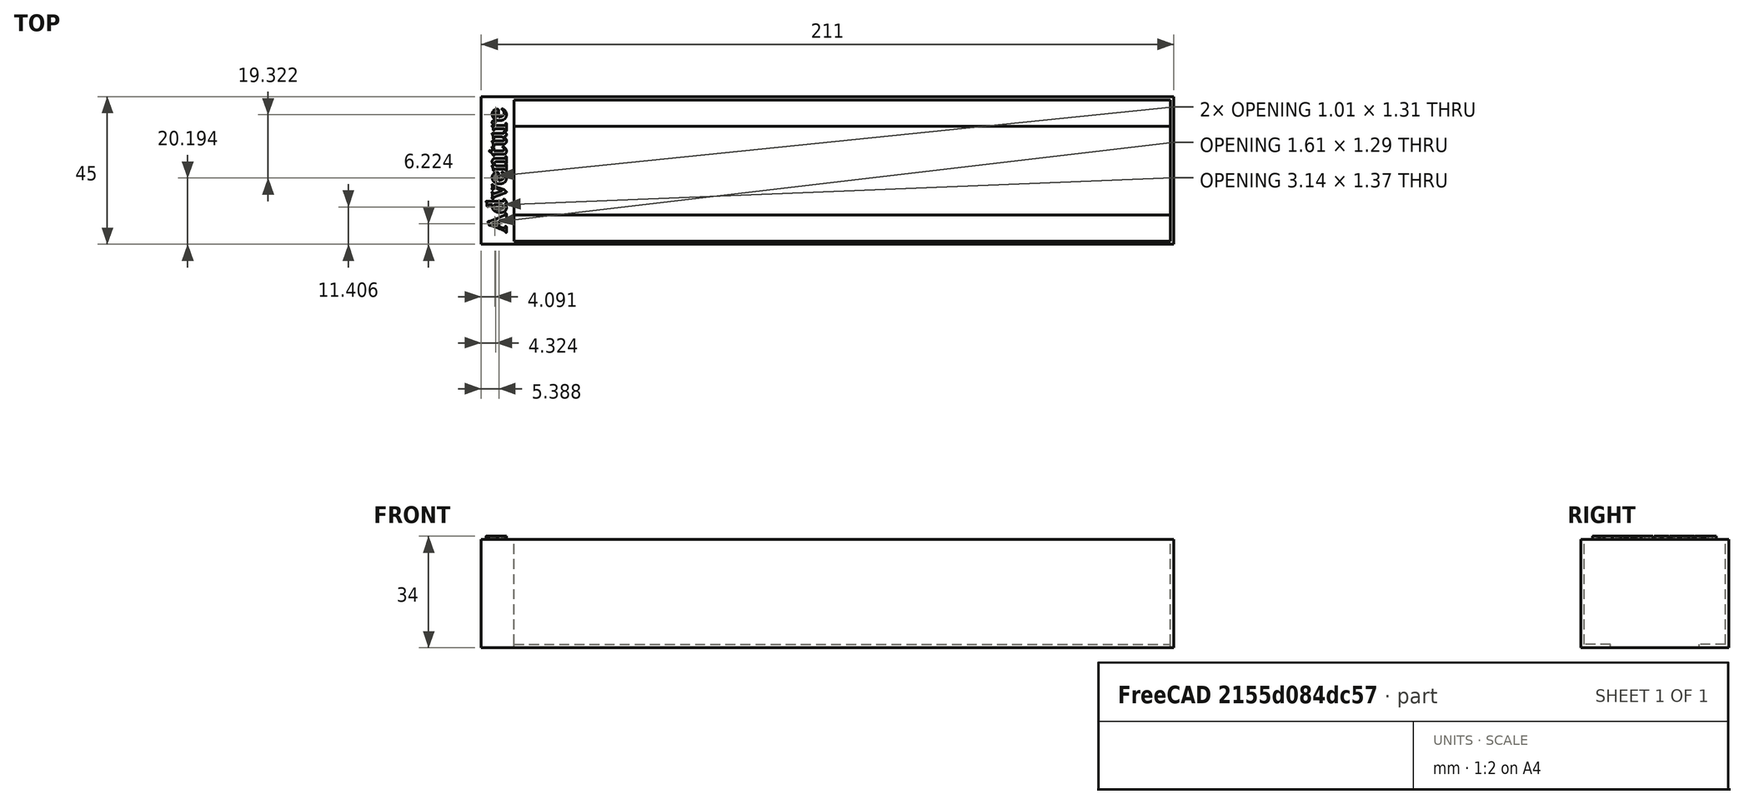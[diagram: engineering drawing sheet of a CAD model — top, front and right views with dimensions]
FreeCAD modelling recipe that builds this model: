
FCSTD DOCUMENT  (FreeCAD 0.18R4 (GitTag))
Label: adventure
License: All rights reserved
LicenseURL: http://en.wikipedia.org/wiki/All_rights_reserved
objects: Part::Box×5, Part::MultiFuse×3, Part::Extrusion×2, Part::Cut×1, Part::Part2DObjectPython×1
note: 12 computed .brp shape members not serialized (recipe doc carries the construction recipe); baked Part::Feature solids carry a one-line shape summary decoded from their .brp

FEATURE [Part::Box] Box  label="Cube"
  AttacherType = Attacher::AttachEngine3D
  Height = 33
  Length = 202
  Placement = pos=(0,-1,0) rot=(0,0,1;0rad)
  Width = 45
FEATURE [Part::Box] Box001  label="Cube001"
  AttacherType = Attacher::AttachEngine3D
  Height = 33
  Length = 200
  Placement = pos=(1,0,0) rot=(0,0,1;0rad)
  Width = 43
FEATURE [Part::Cut] Cut
  Base = -> Box
  Tool = -> Box001
FEATURE [Part::Box] Box002  label="Cube002"
  AttacherType = Attacher::AttachEngine3D
  Height = 1
  Length = 202
  Width = 8
FEATURE [Part::Box] Box003  label="Cube003"
  AttacherType = Attacher::AttachEngine3D
  Height = 1
  Length = 202
  Placement = pos=(0,35,0) rot=(0,0,1;0rad)
  Width = 8
FEATURE [Part::MultiFuse] Fusion
  Shapes = -> [Cut,Box002,Box003]
FEATURE [Part::Box] Box004  label="Cube004"
  AttacherType = Attacher::AttachEngine3D
  Height = 33
  Length = 10
  Placement = pos=(-9,-1,0) rot=(0,0,1;0rad)
  Width = 45
FEATURE [Part::Part2DObjectPython] ShapeString  # Draft 2D object (typed FeaturePython)
  FontFile = <userpath>/Downloads/talisman/Caxton Bold.otf
  Placement = pos=(-1.45,8.11,33) rot=(0,0,1;1.5708rad)
  Size = 3
  String = Adventure
  Tracking = 0
FEATURE [Part::Extrusion] Extrude
  Base = -> ShapeString
  Dir = (0,0,1)
  DirMode = 2
  FaceMakerClass = Part::FaceMakerBullseye
  LengthFwd = 1
  LengthRev = 0
  Solid = false
  Symmetric = false
FEATURE [Part::Extrusion] Extrude001
  Base = -> ShapeString
  Dir = (0,0,1)
  DirMode = 2
  FaceMakerClass = Part::FaceMakerBullseye
  LengthFwd = 1
  LengthRev = 0
  Solid = false
  Symmetric = false
FEATURE [Part::MultiFuse] Fusion001
  Placement = pos=(0,-5.5,0) rot=(0,0,1;0rad)
  Shapes = -> [Extrude001,Extrude]
FEATURE [Part::MultiFuse] Fusion002
  Shapes = -> [Box004,Fusion]
